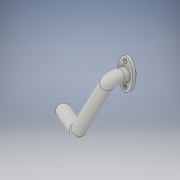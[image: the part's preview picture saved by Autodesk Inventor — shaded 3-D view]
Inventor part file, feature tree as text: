
AUTODESK INVENTOR PART (.ipt)
format: ipt  version: 2018 (Build 220112000, 112)  size: 188,416 bytes
history: native  units: mm
features: sketch x5, plane x2, extrude x1, sweep x1, fillet x1
ambient origin geometry x8: Origin, YZ Plane, XZ Plane, XY Plane, X Axis, Y Axis, Z Axis, Center Point
bodies: Solid1 (feature_tree)
feature tree (10):
  extrude  "Extrusion1"  Depth=6.0mm
  sketch  "Sketch2"  dims[d2=7.0mm d4=3.0mm d5=3.0mm]
  plane  "Work Plane1"
  sketch  "Sketch3"  dims[d6=7.0mm]
  plane  "Work Plane2"
  sweep  "Sweep1"
  fillet  "Fillet1"  Radius=3.0mm
  sketch  "Sketch1"  dims[d0=10.0mm d1=6.0mm]
  sketch  "Sketch4"  dims[d7=7.0mm d8=2.0mm d9=0.0mm d10=2.0mm d11=7.0mm d12=-45.0mm d13=4.487242mm d14=69.478mm d16=15.021mm d17=30.0mm d18=90.0deg d19=8.0mm d20=7.0mm d21=5.0mm d22=5.0mm d23=7.0mm d24=0.0mm d25=0.0mm d26=0.5mm]
  sketch  "3D Sketch1"
